# Revit family: c9e8a6e3-ba43-44e3-86ec-e4f3ceea0630
name_source: partatom
category: Furniture
revit_build: Autodesk Revit 2016 (Build: 20161004_0715(x64)
units: mm (PartAtom-declared; Revit-internal decimal feet)

## family parameters
Always vertical = Yes
Cut with Voids When Loaded = No
OmniClass Number = 23.40.20.11.17
OmniClass Title = Lockers
Room Calculation Point = No
Shared = No
Work Plane-Based = Yes

## types (1)
- See Type Catalog
    Bench Depth = 15"
    Bench Height = 14"
    Brochure = hollman_laminate_lockers_series.pdf
    Default Elevation = 0"
    Depth = 180"
    Description = Lockers
    Height = 864"
    Locker Panel = Wood - Veneer - Hollman - Walnut Clear
    Manufacturer = Hollman Inc
    Model = Double Tier Model B Locker With Bench
    Panel Width = 143 3/4"
    Specifications URL = hollman_laminate locker specs.docx
    URL = http://www.hollman.com
    Unit = Paint - Hollman - Almond
    Width = 144"

## geometry (parser evidence)
native form markers: Blend x4, Sweep x17
no freeform markers — native parametric forms only
